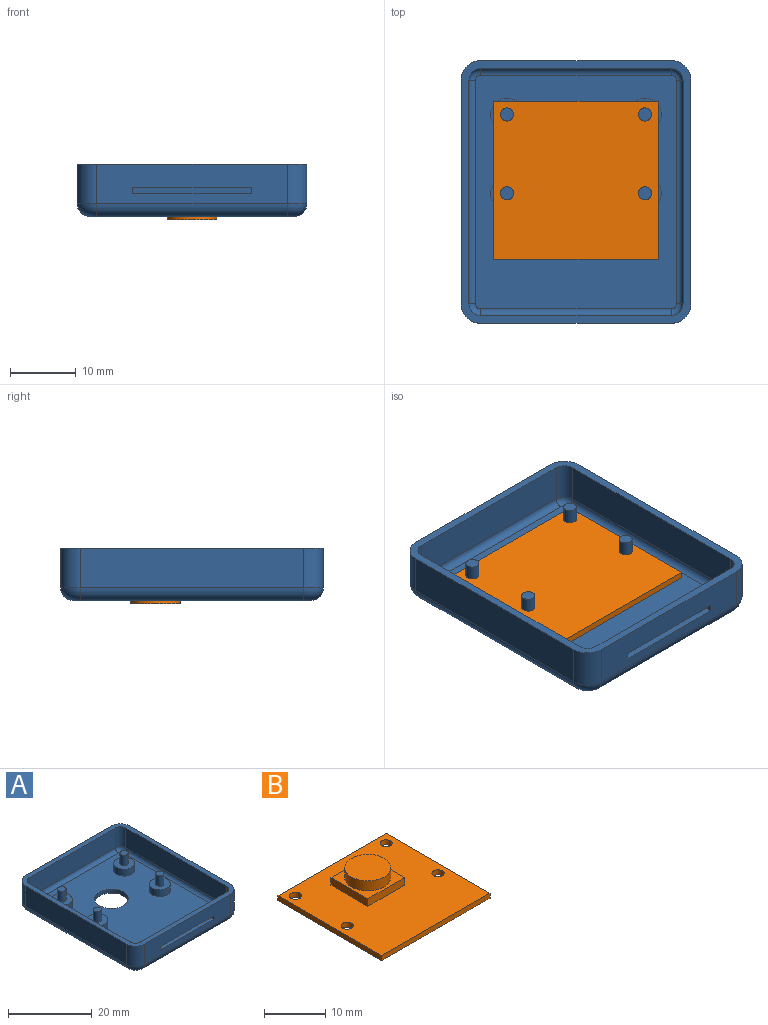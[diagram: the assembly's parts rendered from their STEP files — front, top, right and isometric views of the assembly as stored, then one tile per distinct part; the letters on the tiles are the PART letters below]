
ASSEMBLY  parts=2 mates=1
PART A: 57 faces, bbox 35x40x8 mm
  f0: plane 29x6mm, normal (0,-1,0), area 156mm2, adj f2,f7,f10,f36,f37,f38,f39,f47
  f1: plane 35.6x30.6mm, normal (0,0,1), area 960mm2, adj f19,f20,f24,f28,f32,f49,f50,f51
  f2: plane 40x35mm, normal (0,0,1), area 169.3mm2, adj f0,f3,f4,f5,f7,f8,f9,f10
  f3: plane 34x6mm, normal (1,0,0), area 204mm2, adj f2,f7,f8,f46
  f4: plane 29x6mm, normal (0,1,0), area 174mm2, adj f2,f8,f9,f42
  f5: plane 34x6mm, normal (-1,0,0), area 204mm2, adj f2,f9,f10,f43
  f6: plane 36x31mm, normal (0,0,-1), area 1064.9mm2, adj f19,f41,f42,f43,f44,f45,f46,f47
  f7: cylinder r=3mm len=6mm, axis (0,0,1), area 28.3mm2, adj f0,f2,f3,f48
  f8: cylinder r=3mm len=6mm, axis (0,0,-1), area 28.3mm2, adj f2,f3,f4,f44
  f9: cylinder r=3mm len=6mm, axis (0,0,1), area 28.3mm2, adj f2,f4,f5,f41
  f10: cylinder r=3mm len=6mm, axis (0,0,-1), area 28.3mm2, adj f0,f2,f5,f45
  f11: plane 29x5.8mm, normal (0,1,0), area 168.2mm2, adj f2,f15,f18,f49
  f12: plane 34x5.8mm, normal (-1,0,0), area 197.2mm2, adj f2,f15,f16,f52
  f13: plane 29x5.8mm, normal (0,-1,0), area 168.2mm2, adj f2,f16,f17,f56
  f14: plane 34x5.8mm, normal (1,0,0), area 197.2mm2, adj f2,f17,f18,f53
  f15: cylinder r=1.8mm len=5.8mm, axis (0,0,1), area 16.4mm2, adj f2,f11,f12,f50
  f16: cylinder r=1.8mm len=5.8mm, axis (0,0,-1), area 16.4mm2, adj f2,f12,f13,f54
  f17: cylinder r=1.8mm len=5.8mm, axis (0,0,1), area 16.4mm2, adj f2,f13,f14,f55
  f18: cylinder r=1.8mm len=5.8mm, axis (0,0,-1), area 16.4mm2, adj f2,f11,f14,f51
  f19: cylinder r=4mm len=8mm, axis (0,0,1), area 30.2mm2, adj f1,f6
  f20: cylinder r=2.5mm len=5mm, axis (0,0,-1), area 31.4mm2, adj f1,f21
  f21: plane 5x5mm, normal (0,0,1), area 16.5mm2, adj f20,f23
  f22: plane 2x2mm, normal (0,0,1), area 3.1mm2, adj f23
  f23: cylinder r=1mm len=3mm, axis (0,0,-1), area 18.8mm2, adj f21,f22
  f24: cylinder r=2.5mm len=5mm, axis (0,0,-1), area 31.4mm2, adj f1,f25
  f25: plane 5x5mm, normal (0,0,1), area 16.5mm2, adj f24,f27
  f26: plane 2x2mm, normal (0,0,1), area 3.1mm2, adj f27
  f27: cylinder r=1mm len=3mm, axis (0,0,-1), area 18.8mm2, adj f25,f26
  f28: cylinder r=2.5mm len=5mm, axis (0,0,-1), area 31.4mm2, adj f1,f29
  f29: plane 5x5mm, normal (0,0,1), area 16.5mm2, adj f28,f31
  f30: plane 2x2mm, normal (0,0,1), area 3.1mm2, adj f31
  f31: cylinder r=1mm len=3mm, axis (0,0,-1), area 18.8mm2, adj f29,f30
  f32: cylinder r=2.5mm len=5mm, axis (0,0,-1), area 31.4mm2, adj f1,f33
  f33: plane 5x5mm, normal (0,0,1), area 16.5mm2, adj f32,f35
  f34: plane 2x2mm, normal (0,0,1), area 3.1mm2, adj f35
  f35: cylinder r=1mm len=3mm, axis (0,0,-1), area 18.8mm2, adj f33,f34
  f36: plane 18x1mm, normal (0,0,1), area 18mm2, adj f0,f37,f39,f40
  f37: plane 1x1mm, normal (-1,0,0), area 1mm2, adj f0,f36,f38,f40
  f38: plane 18x1mm, normal (0,0,-1), area 18mm2, adj f0,f37,f39,f40
  f39: plane 1x1mm, normal (1,0,0), area 1mm2, adj f0,f36,f38,f40
  f40: plane 18x1mm, normal (0,-1,0), area 18mm2, adj f36,f37,f38,f39
  f41: torus R=1mm, axis (0,0,1), area 11.2mm2, adj f6,f9,f42,f43
  f42: cylinder r=2mm len=29mm, axis (-1,0,0), area 91.1mm2, adj f4,f6,f41,f44
  f43: cylinder r=2mm len=34mm, axis (0,-1,0), area 106.8mm2, adj f5,f6,f41,f45
  f44: torus R=1mm, axis (0,0,1), area 11.2mm2, adj f6,f8,f42,f46
  f45: torus R=1mm, axis (0,0,1), area 11.2mm2, adj f6,f10,f43,f47
  f46: cylinder r=2mm len=34mm, axis (0,1,0), area 106.8mm2, adj f3,f6,f44,f48
  f47: cylinder r=2mm len=29mm, axis (1,0,0), area 91.1mm2, adj f0,f6,f45,f48
  f48: torus R=1mm, axis (0,0,1), area 11.2mm2, adj f6,f7,f46,f47
  f49: cylinder r=1mm len=29mm, axis (-1,0,0), area 45.6mm2, adj f1,f11,f50,f51
  f50: torus R=0.8mm, axis (0,0,1), area 3.5mm2, adj f1,f15,f49,f52
  f51: torus R=0.8mm, axis (0,0,1), area 3.5mm2, adj f1,f18,f49,f53
  f52: cylinder r=1mm len=34mm, axis (0,-1,0), area 53.4mm2, adj f1,f12,f50,f54
  f53: cylinder r=1mm len=34mm, axis (0,1,0), area 53.4mm2, adj f1,f14,f51,f55
  f54: torus R=0.8mm, axis (0,0,1), area 3.5mm2, adj f1,f16,f52,f56
  f55: torus R=0.8mm, axis (0,0,1), area 3.5mm2, adj f1,f17,f53,f56
  f56: cylinder r=1mm len=29mm, axis (1,0,0), area 45.6mm2, adj f1,f13,f54,f55
PART B: 17 faces, bbox 25x24x4.5 mm
  f0: plane 25x24mm, normal (0,0,1), area 515.2mm2, adj f1,f2,f3,f4,f5,f6,f7,f8
  f1: plane 25x1mm, normal (0,-1,0), area 25mm2, adj f0,f2,f8,f9
  f2: plane 24x1mm, normal (1,0,0), area 24mm2, adj f0,f1,f3,f9
  f3: plane 25x1mm, normal (0,1,0), area 25mm2, adj f0,f2,f8,f9
  f4: cylinder r=1mm len=2mm, axis (0,0,-1), area 6.3mm2, adj f0,f9
  f5: cylinder r=1mm len=2mm, axis (0,0,-1), area 6.3mm2, adj f0,f9
  f6: cylinder r=1mm len=2mm, axis (0,0,-1), area 6.3mm2, adj f0,f9
  f7: cylinder r=1mm len=2mm, axis (0,0,-1), area 6.3mm2, adj f0,f9
  f8: plane 24x1mm, normal (-1,0,0), area 24mm2, adj f0,f1,f3,f9
  f9: plane 25x24mm, normal (0,0,-1), area 587.4mm2, adj f1,f2,f3,f4,f5,f6,f7,f8
  f10: plane 8.5x1.5mm, normal (0,-1,0), area 12.7mm2, adj f0,f11,f13,f14
  f11: plane 8.5x1.5mm, normal (1,0,0), area 12.8mm2, adj f0,f10,f12,f14
  f12: plane 8.5x1.5mm, normal (0,1,0), area 12.7mm2, adj f0,f11,f13,f14
  f13: plane 8.5x1.5mm, normal (-1,0,0), area 12.8mm2, adj f0,f10,f12,f14
  f14: plane 8.5x8.5mm, normal (0,0,1), area 28.1mm2, adj f10,f11,f12,f13,f15
  f15: cylinder r=3.75mm len=7.5mm, axis (0,0,-1), area 47.1mm2, adj f14,f16
  f16: plane 7.5x7.5mm, normal (0,0,1), area 44.2mm2, adj f15
PLACE A at identity fixed
PLACE B rot(axis=(0,1,0),180deg) t=(-104.48,0,4)mm
MATE parallel A.f28 <-> B.f4  axis (0,0,1) through (-64.22,24.68,3.2)mm
